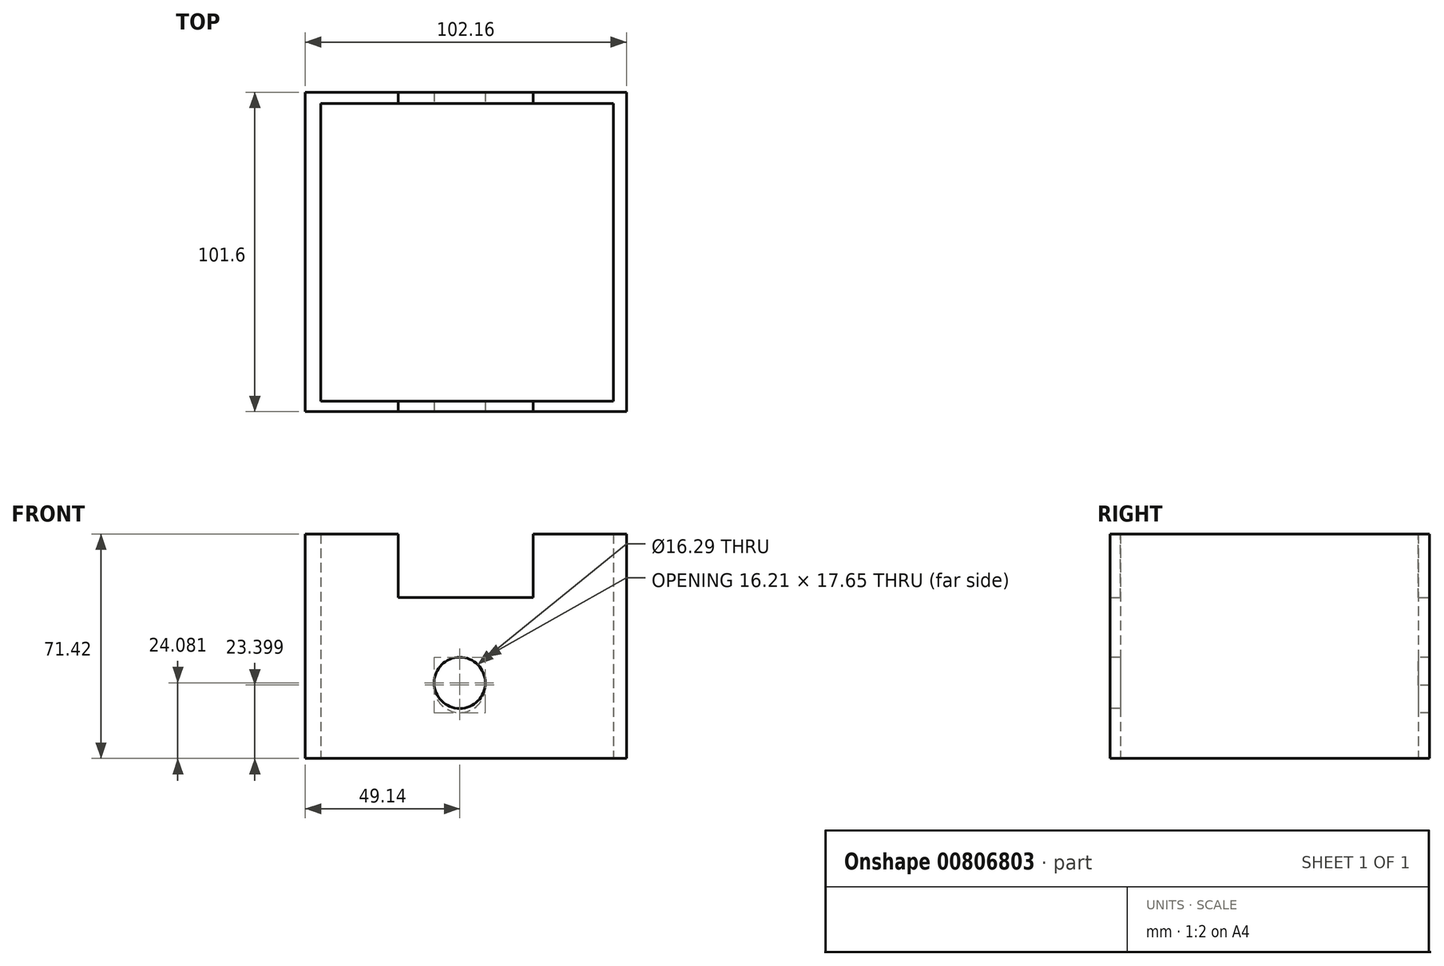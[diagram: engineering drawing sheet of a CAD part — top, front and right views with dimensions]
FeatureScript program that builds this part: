
annotation { "Feature Type Name" : "Feature", "Feature Type Description" : "" }
export const myFeature = defineFeature(function(context is Context, id is Id, definition is map)
    precondition{}
    {
        {
            var Q0;
            Q0=qCreatedBy(makeId("Front.planeOp"),FACE);
            var sketch = newSketch(context, id + "F0", { "sketchPlane" : qUnion([Q0])});
            skLineSegment(sketch, "E0.bottom", {"start": v(-19.52, 13.42) * mm, "end": v(23.4, 13.42) * mm});
            skLineSegment(sketch, "E0.top", {"start": v(-49.14, -37.8) * mm, "end": v(53.02, -37.8) * mm});
            skLineSegment(sketch, "E0.left", {"start": v(-49.14, 13.42) * mm, "end": v(-49.14, -37.8) * mm});
            skLineSegment(sketch, "E0.right", {"start": v(53.02, 13.42) * mm, "end": v(53.02, -37.8) * mm});
            skLineSegment(sketch, "E1.bottom", {"start": v(23.4, 33.63) * mm, "end": v(53.02, 33.63) * mm});
            skLineSegment(sketch, "E1.left", {"start": v(23.4, 33.63) * mm, "end": v(23.4, 13.42) * mm});
            skLineSegment(sketch, "E1.right", {"start": v(53.02, 33.63) * mm, "end": v(53.02, 13.42) * mm});
            skLineSegment(sketch, "E2.top", {"start": v(-49.14, 33.63) * mm, "end": v(-19.52, 33.63) * mm});
            skLineSegment(sketch, "E2.left", {"start": v(-49.14, 13.42) * mm, "end": v(-49.14, 33.63) * mm});
            skLineSegment(sketch, "E2.right", {"start": v(-19.52, 13.42) * mm, "end": v(-19.52, 33.63) * mm});
            skSolve(sketch);
        }
        {
            var Q0;
            Q0=makeQuery(id+"F0.imprint","IMPRINT",FACE,{"disambiguationData":[TD([[makeQuery(id+"F0.imprint","IMPRINT",EDGE,{"derivedFrom":sQuery(id+"F0.wireOp",EDGE,"E0.bottom")}),-1.0]])]});
            extrude(context, id + "F1", {"entities" : qUnion([Q0]), "endBound" : BoundingType.SYMMETRIC, "depth" : 101.6 * mm, "offsetDistance" : 25.4 * mm});
        }
        {
            var Q0;
            Q0=qCreatedBy(makeId("Top.planeOp"),FACE);
            var sketch = newSketch(context, id + "F2", { "sketchPlane" : qUnion([Q0])});
            skLineSegment(sketch, "E3.bottom", {"start": v(-44.16, 47.2) * mm, "end": v(48.86, 47.2) * mm});
            skLineSegment(sketch, "E3.top", {"start": v(-44.16, -47.48) * mm, "end": v(48.86, -47.48) * mm});
            skLineSegment(sketch, "E3.left", {"start": v(-44.16, 47.2) * mm, "end": v(-44.16, -47.48) * mm});
            skLineSegment(sketch, "E3.right", {"start": v(48.86, 47.2) * mm, "end": v(48.86, -47.48) * mm});
            skSolve(sketch);
        }
        {
            var Q0;
            Q0 = qSketchRegion(id + "F2", true);
            extrude(context, id + "F3", {"entities" : qUnion([Q0]), "operationType" : NewBodyOperationType.REMOVE, "endBound" : BoundingType.SYMMETRIC, "depth" : 228.6 * mm, "offsetDistance" : 25.4 * mm});
        }
        {
            var Q0;
            Q0=qCreatedBy(makeId("Front.planeOp"),FACE);
            var sketch = newSketch(context, id + "F4", { "sketchPlane" : qUnion([Q0])});
            skCircle(sketch, "E4", {"center": v(0, -15.1) * mm, "radius": 8.12 * mm});
            skSolve(sketch);
        }
        {
            var Q0;
            Q0 = qSketchRegion(id + "F4", true);
            extrude(context, id + "F5", {"entities" : qUnion([Q0]), "operationType" : NewBodyOperationType.REMOVE, "oppositeDirection" : true, "depth" : 228.6 * mm, "offsetDistance" : 25.4 * mm});
        }
        {
            var Q0;
            Q0=makeQuery(id+"F1.opExtrude","CAP_FACE",FACE,{"disambiguationData":[OSD([sQuery(id+"F0.wireOp",EDGE,"E0.bottom"),sQuery(id+"F0.wireOp",EDGE,"E0.top"),sQuery(id+"F0.wireOp",EDGE,"E0.left"),sQuery(id+"F0.wireOp",EDGE,"E0.right"),sQuery(id+"F0.wireOp",EDGE,"E1.bottom"),sQuery(id+"F0.wireOp",EDGE,"E1.left"),sQuery(id+"F0.wireOp",EDGE,"E1.right"),sQuery(id+"F0.wireOp",EDGE,"E2.top"),sQuery(id+"F0.wireOp",EDGE,"E2.left"),sQuery(id+"F0.wireOp",EDGE,"E2.right")])],"isStart":false});
            var sketch = newSketch(context, id + "F6", { "sketchPlane" : qUnion([Q0])});
            skCircle(sketch, "E5", {"center": v(0, -13.7) * mm, "radius": 8.14 * mm});
            skSolve(sketch);
        }
        {
            var Q0;
            Q0=makeQuery(id+"F6.imprint","IMPRINT",FACE,{"disambiguationData":[TD([[makeQuery(id+"F6.imprint","IMPRINT",EDGE,{"derivedFrom":sQuery(id+"F6.wireOp",EDGE,"E5")}),1.0]])]});
            extrude(context, id + "F7", {"entities" : qUnion([Q0]), "operationType" : NewBodyOperationType.REMOVE, "oppositeDirection" : true, "depth" : 152.4 * mm, "offsetDistance" : 25.4 * mm});
        }
    });
